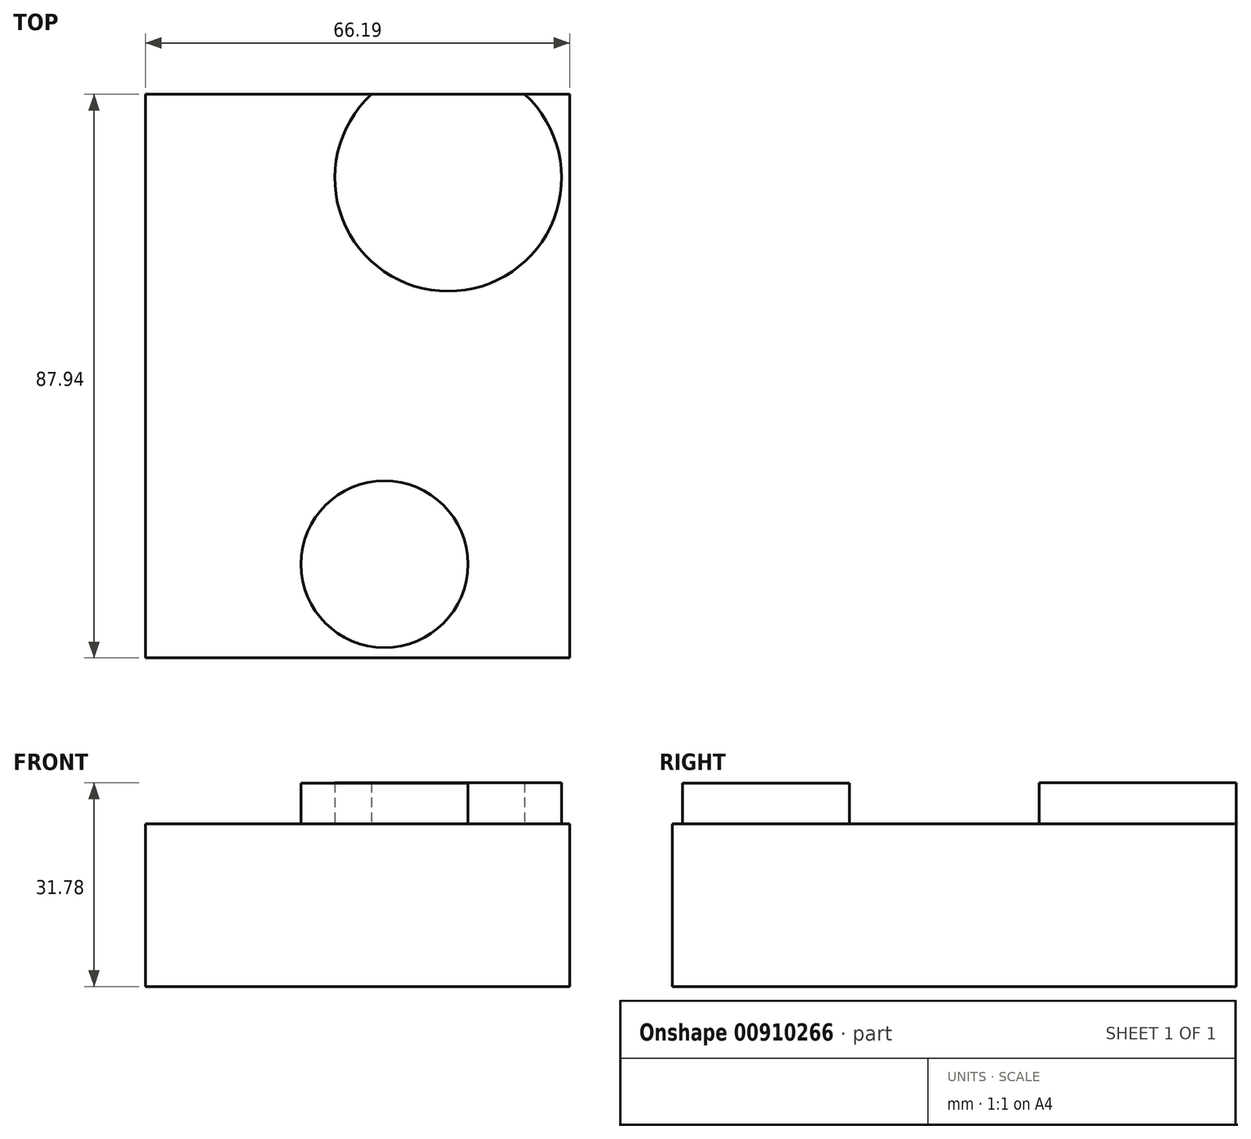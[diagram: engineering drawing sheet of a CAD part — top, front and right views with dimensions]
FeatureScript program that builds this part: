
annotation { "Feature Type Name" : "Feature", "Feature Type Description" : "" }
export const myFeature = defineFeature(function(context is Context, id is Id, definition is map)
    precondition{}
    {
        {
            var Q0;
            Q0=qCreatedBy(makeId("Top.planeOp"),FACE);
            var sketch = newSketch(context, id + "F0", { "sketchPlane" : qUnion([Q0])});
            skLineSegment(sketch, "E0.bottom", {"start": v(-37.29, 46.3) * mm, "end": v(28.9, 46.3) * mm});
            skLineSegment(sketch, "E0.top", {"start": v(-37.29, -41.64) * mm, "end": v(28.9, -41.64) * mm});
            skLineSegment(sketch, "E0.left", {"start": v(-37.29, 46.3) * mm, "end": v(-37.29, -41.64) * mm});
            skLineSegment(sketch, "E0.right", {"start": v(28.9, 46.3) * mm, "end": v(28.9, -41.64) * mm});
            skSolve(sketch);
        }
        {
            var Q0;
            Q0 = qSketchRegion(id + "F0", true);
            extrude(context, id + "F1", {"entities" : qUnion([Q0]), "depth" : 25.4 * mm, "offsetDistance" : 25.4 * mm});
        }
        {
            var Q0;
            Q0=makeQuery(id+"F1.opExtrude","CAP_FACE",FACE,{"disambiguationData":[OSD([sQuery(id+"F0.wireOp",EDGE,"E0.bottom"),sQuery(id+"F0.wireOp",EDGE,"E0.top"),sQuery(id+"F0.wireOp",EDGE,"E0.left"),sQuery(id+"F0.wireOp",EDGE,"E0.right")])],"isStart":false});
            var sketch = newSketch(context, id + "F2", { "sketchPlane" : qUnion([Q0])});
            skCircle(sketch, "E1", {"center": v(0, -27.03) * mm, "radius": 13.01 * mm});
            skCircle(sketch, "E2", {"center": v(9.94, 33.25) * mm, "radius": 17.69 * mm});
            skSolve(sketch);
        }
        {
            var Q0;
            Q0=makeQuery(id+"F2.imprint","IMPRINT",FACE,{"disambiguationData":[TD([[makeQuery(id+"F2.imprint","IMPRINT",EDGE,{"derivedFrom":sQuery(id+"F2.wireOp",EDGE,"E1")}),1.0]])]});
            extrude(context, id + "F3", {"entities" : qUnion([Q0]), "operationType" : NewBodyOperationType.ADD, "depth" : 6.35 * mm, "offsetDistance" : 25.4 * mm});
        }
        {
            var Q0;
            {var subQ0=sQuery(id+"F2.wireOp",EDGE,"E2");var subQ1=makeQuery(id+"F1.opExtrude","CAP_EDGE",EDGE,{"disambiguationData":[OSD([sQuery(id+"F0.wireOp",EDGE,"E0.bottom")])],"isStart":false});var subQ2=makeQuery(id+"F2.imprint","INTERSECT",VERTEX,{"disambiguationData":[OD(0.0)],"derivedFrom":[subQ1,subQ0]});Q0=makeQuery(id+"F2.imprint","IMPRINT",FACE,{"disambiguationData":[TD([[makeQuery(id+"F2.imprint","IMPRINT",EDGE,{"disambiguationData":[TD([[subQ2,-1.0]])],"derivedFrom":subQ0}),1.0]])]});}
            extrude(context, id + "F4", {"entities" : qUnion([Q0]), "operationType" : NewBodyOperationType.ADD, "depth" : 6.38 * mm, "offsetDistance" : 25.4 * mm});
        }
    });
